# Revit family: Soap-Dispenser_Commercial_TES1ADC-05_TOTO
name_source: partatom
category: Furniture
revit_build: Autodesk Revit Architecture 2013 (Build: 20130531_2115(x64)
units: mm (PartAtom-declared; Revit-internal decimal feet)

## types (1)
- TES1ADC-05
    04 CSI = 22 42 39
    95 CSI = 15416
    ADA Compliant = Yes
    Apparent Power = 10 VA
    Assembly Code = C1030200
    CAD Drawing URL = http://assets.totousa.com
    Color Availability = #CP Polished Chrome, #BN Brushed Nickel, #PN Polished Nickel
    Default Elevation = 48"
    Depth = 3"
    Description = Sensor Operated Soap Dispenser
    Finish = Metal - TOTO - Chrome - Polished
    Frequency = 60 Hz
    Height = 5 17/32"
    Manufacturer = TOTO USA, Inc.
    Manufacturer Fax = (770) 282-0002
    Model = TES1ADC-05
    Number of Poles = 1
    Phase = 1
    Shipping Weight = 0.00 lb
    Spec Sheet URL = http://assets.totousa.com
    Style = Commercial
    Subcategory = Accessories
    Toto BIM Number = BM-00209
    URL = http://www.totousa.com
    Voltage = 120 V
    Warranty = Three Year Limited Warranty
    Warranty URL = http://www.totousa.com
    Width = 1 149/256"

## geometry (parser evidence)
native form markers: Blend x24, Sweep x1
no freeform markers — native parametric forms only
